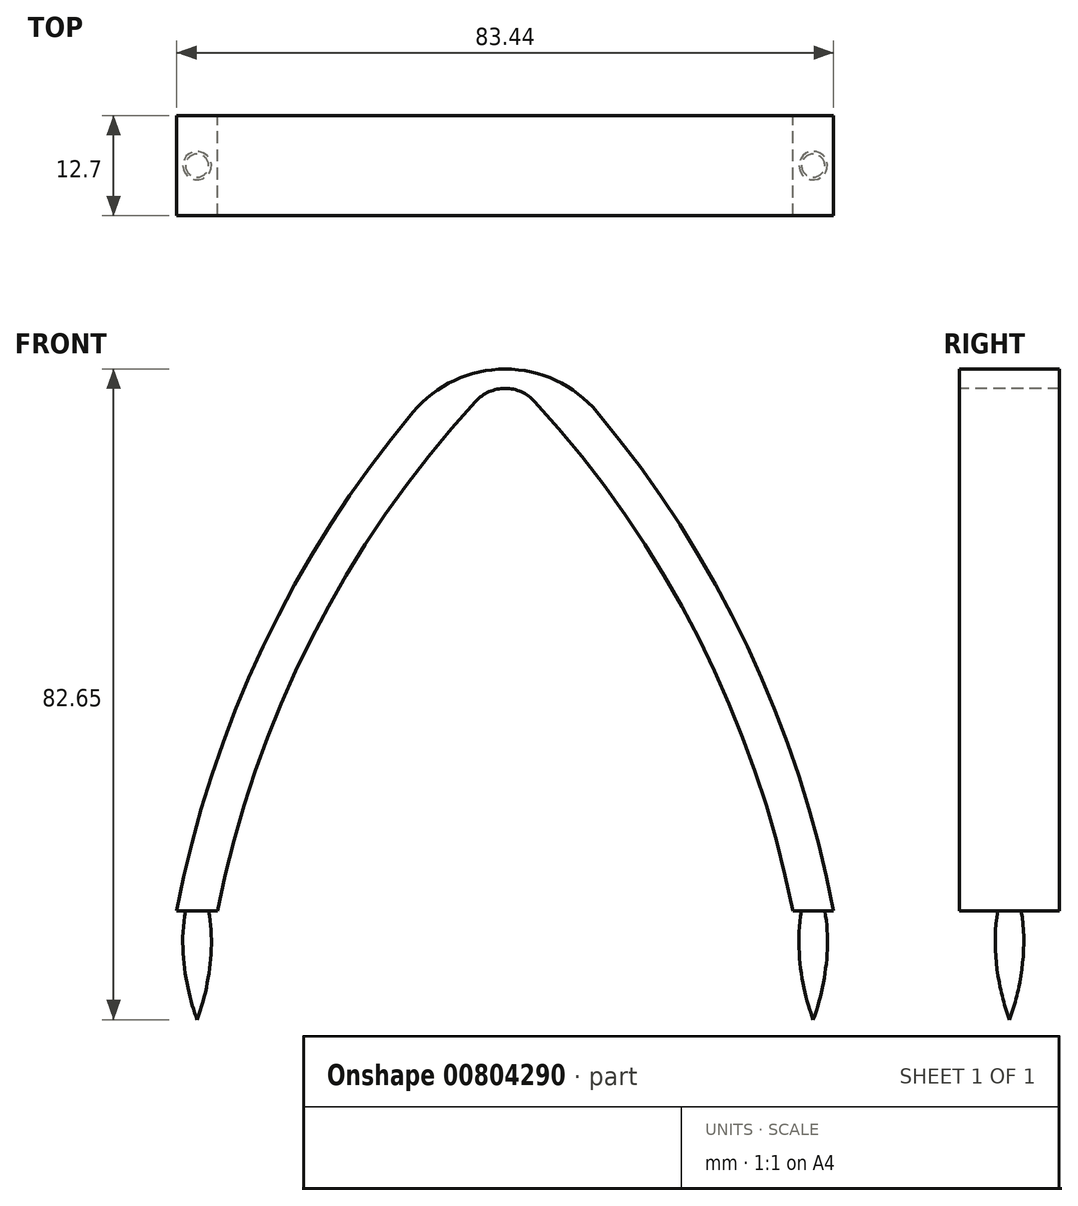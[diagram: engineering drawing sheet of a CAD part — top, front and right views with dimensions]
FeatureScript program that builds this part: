
annotation { "Feature Type Name" : "Feature", "Feature Type Description" : "" }
export const myFeature = defineFeature(function(context is Context, id is Id, definition is map)
    precondition{}
    {
        {
            var Q0;
            Q0=qCreatedBy(makeId("Front.planeOp"),FACE);
            var sketch = newSketch(context, id + "F0", { "sketchPlane" : qUnion([Q0])});
            skArc(sketch, "E0", {"start": v(0, 76.57) * mm, "mid": v(-26.88, 42.01) * mm, "end": v(-41.72, 0.83) * mm});
            skArc(sketch, "E1", {"start": v(41.72, 0.83) * mm, "mid": v(26.88, 42.01) * mm, "end": v(0, 76.57) * mm});
            skArc(sketch, "E2.0", {"start": v(0, 69.5) * mm, "mid": v(-23.35, 37.86) * mm, "end": v(-36.54, 0.83) * mm});
            skArc(sketch, "E2.1", {"start": v(36.54, 0.83) * mm, "mid": v(23.35, 37.86) * mm, "end": v(0, 69.5) * mm});
            skLineSegment(sketch, "E3", {"start": v(-41.72, 0.83) * mm, "end": v(-36.54, 0.83) * mm});
            skLineSegment(sketch, "E4", {"start": v(36.54, 0.83) * mm, "end": v(41.72, 0.83) * mm});
            skSolve(sketch);
        }
        {
            var Q0;
            Q0=makeQuery(id+"F0.imprint","IMPRINT",FACE,{"disambiguationData":[TD([[makeQuery(id+"F0.imprint","IMPRINT",EDGE,{"derivedFrom":sQuery(id+"F0.wireOp",EDGE,"E0")}),1.0]])]});
            extrude(context, id + "F1", {"entities" : qUnion([Q0]), "depth" : 12.7 * mm, "offsetDistance" : 25.4 * mm});
        }
        {
            var Q0;
            Q0=makeQuery(id+"F1.opExtrude","SWEPT_EDGE",EDGE,{"disambiguationData":[OSD([sQuery(id+"F0.wireOp",EDGE,"E0"),sQuery(id+"F0.wireOp",EDGE,"E1")])]});
            fillet(context, id + "F2", {"entities" : qUnion([Q0]), "radius" : 15.24 * mm, "tangentPropagation" : true, "allowEdgeOverflow" : false});
        }
        {
            var Q0;
            Q0=makeQuery(id+"F1.opExtrude","SWEPT_EDGE",EDGE,{"disambiguationData":[OSD([sQuery(id+"F0.wireOp",EDGE,"E2.0"),sQuery(id+"F0.wireOp",EDGE,"E2.1")])]});
            fillet(context, id + "F3", {"entities" : qUnion([Q0]), "radius" : 5.08 * mm, "tangentPropagation" : true, "allowEdgeOverflow" : false});
        }
        {
            var Q0;
            Q0=qCreatedBy(makeId("Front.planeOp"),FACE);
            cPlane(context, id + "F4", {"entities" : qUnion([Q0]), "cplaneType" : CPlaneType.OFFSET, "offset" : 6.35 * mm, "width" : 152.4 * mm, "height" : 152.4 * mm});
        }
        {
            var Q0;
            Q0=qCreatedBy(id+"F4.planeOp",FACE);
            var sketch = newSketch(context, id + "F5", { "sketchPlane" : qUnion([Q0])});
            skFitSpline(sketch, "E5", {"points": [v(-40.6, 0.83) * mm, v(-39.13, -12.97) * mm], "startDerivative": vector(-2.88, -15.05) * mm, "endDerivative": vector(3.58, -9.42) * mm});
            skLineSegment(sketch, "E6", {"start": v(-39.13, -12.97) * mm, "end": v(-39.13, 0.83) * mm});
            skLineSegment(sketch, "E7", {"start": v(-40.6, 0.83) * mm, "end": v(-39.13, 0.83) * mm});
            skFitSpline(sketch, "E8", {"points": [v(37.66, 0.83) * mm, v(39.13, -12.97) * mm], "startDerivative": vector(-2.88, -15.05) * mm, "endDerivative": vector(3.58, -9.42) * mm});
            skLineSegment(sketch, "E9", {"start": v(39.13, -12.97) * mm, "end": v(39.13, 0.83) * mm});
            skLineSegment(sketch, "E10", {"start": v(37.66, 0.83) * mm, "end": v(39.13, 0.83) * mm});
            skSolve(sketch);
        }
        {
            var Q0;
            Q0=makeQuery(id+"F5.imprint","IMPRINT",FACE,{"disambiguationData":[TD([[makeQuery(id+"F5.imprint","IMPRINT",EDGE,{"derivedFrom":sQuery(id+"F5.wireOp",EDGE,"E8")}),1.0]])]});
            var Q1;
            Q1=sQuery(id+"F5.wireOp",EDGE,"E9");
            revolve(context, id + "F6", {"operationType" : NewBodyOperationType.ADD, "surfaceOperationType" : NewSurfaceOperationType.NEW, "entities" : qUnion([Q0]), "axis" : qUnion([Q1]), "revolveType" : RevolveType.FULL});
        }
        {
            var Q0;
            Q0=makeQuery(id+"F5.imprint","IMPRINT",FACE,{"disambiguationData":[TD([[makeQuery(id+"F5.imprint","IMPRINT",EDGE,{"derivedFrom":sQuery(id+"F5.wireOp",EDGE,"E5")}),1.0]])]});
            var Q1;
            Q1=sQuery(id+"F5.wireOp",EDGE,"E6");
            revolve(context, id + "F7", {"operationType" : NewBodyOperationType.ADD, "surfaceOperationType" : NewSurfaceOperationType.NEW, "entities" : qUnion([Q0]), "axis" : qUnion([Q1]), "revolveType" : RevolveType.FULL});
        }
    });
